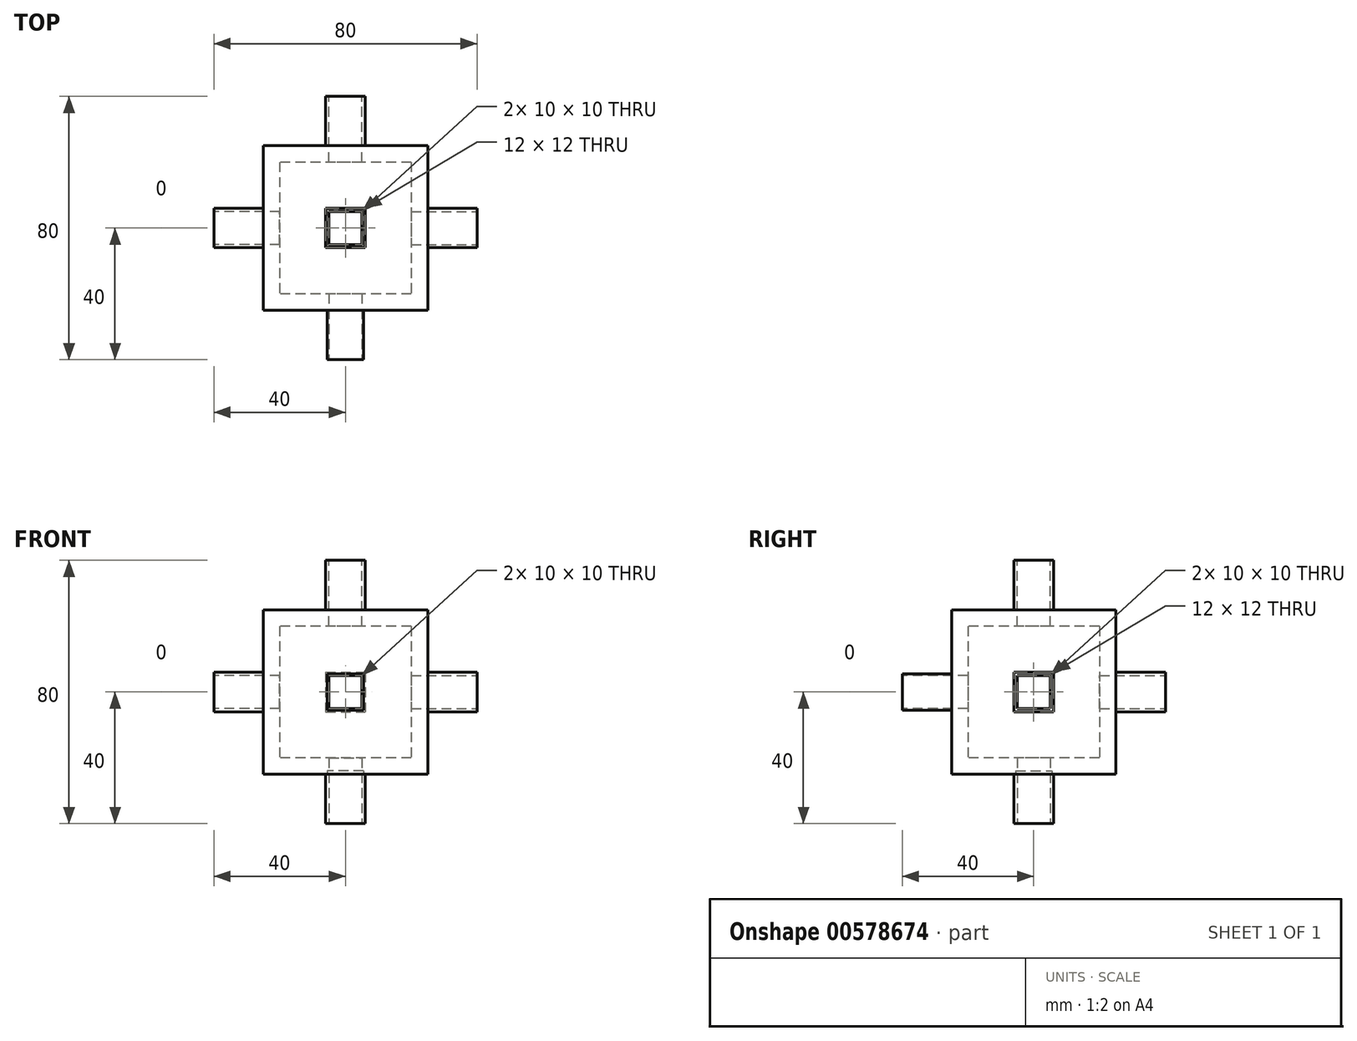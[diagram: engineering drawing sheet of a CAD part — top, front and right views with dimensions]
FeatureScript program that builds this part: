
annotation { "Feature Type Name" : "Feature", "Feature Type Description" : "" }
export const myFeature = defineFeature(function(context is Context, id is Id, definition is map)
    precondition{}
    {
        {
            var Q0;
            Q0=qCreatedBy(makeId("Top.planeOp"),FACE);
            var sketch = newSketch(context, id + "F0", { "sketchPlane" : qUnion([Q0])});
            skLineSegment(sketch, "E0.bottom", {"start": v(25, 25) * mm, "end": v(-25, 25) * mm});
            skLineSegment(sketch, "E0.top", {"start": v(25, -25) * mm, "end": v(-25, -25) * mm});
            skLineSegment(sketch, "E0.left", {"start": v(25, 25) * mm, "end": v(25, -25) * mm});
            skLineSegment(sketch, "E0.right", {"start": v(-25, 25) * mm, "end": v(-25, -25) * mm});
            skPoint(sketch, "E0.middle", {"position": v(0, 0) * mm});
            skLineSegment(sketch, "E1.0", {"start": v(20, -20) * mm, "end": v(-20, -20) * mm});
            skLineSegment(sketch, "E1.1", {"start": v(20, 20) * mm, "end": v(20, -20) * mm});
            skLineSegment(sketch, "E1.2", {"start": v(20, 20) * mm, "end": v(-20, 20) * mm});
            skLineSegment(sketch, "E1.3", {"start": v(-20, 20) * mm, "end": v(-20, -20) * mm});
            skSolve(sketch);
        }
        {
            var Q0;
            Q0=makeQuery(id+"F0.imprint","IMPRINT",FACE,{"disambiguationData":[TD([[makeQuery(id+"F0.imprint","IMPRINT",EDGE,{"derivedFrom":sQuery(id+"F0.wireOp",EDGE,"E0.bottom")}),1.0]])]});
            extrude(context, id + "F1", {"entities" : qUnion([Q0]), "depth" : 50 * mm, "offsetDistance" : 25 * mm});
        }
        {
            var Q0;
            Q0=makeQuery(id+"F0.imprint","IMPRINT",FACE,{"disambiguationData":[TD([[makeQuery(id+"F0.imprint","IMPRINT",EDGE,{"derivedFrom":sQuery(id+"F0.wireOp",EDGE,"E1.0")}),-1.0]])]});
            extrude(context, id + "F2", {"entities" : qUnion([Q0]), "operationType" : NewBodyOperationType.ADD, "depth" : 5 * mm, "offsetDistance" : 25 * mm});
        }
        {
            var Q0;
            Q0=makeQuery(id+"F1.opExtrude","CAP_FACE",FACE,{"disambiguationData":[OSD([sQuery(id+"F0.wireOp",EDGE,"E0.bottom"),sQuery(id+"F0.wireOp",EDGE,"E0.top"),sQuery(id+"F0.wireOp",EDGE,"E0.left"),sQuery(id+"F0.wireOp",EDGE,"E0.right"),sQuery(id+"F0.wireOp",EDGE,"E1.0"),sQuery(id+"F0.wireOp",EDGE,"E1.1"),sQuery(id+"F0.wireOp",EDGE,"E1.2"),sQuery(id+"F0.wireOp",EDGE,"E1.3")])],"isStart":false});
            var sketch = newSketch(context, id + "F3", { "sketchPlane" : qUnion([Q0])});
            skLineSegment(sketch, "E2.0", {"start": v(20, -20) * mm, "end": v(-20, -20) * mm});
            skLineSegment(sketch, "E3.0", {"start": v(-20, 20) * mm, "end": v(-20, -20) * mm});
            skLineSegment(sketch, "E4.0", {"start": v(20, 20) * mm, "end": v(-20, 20) * mm});
            skLineSegment(sketch, "E5.0", {"start": v(20, 20) * mm, "end": v(20, -20) * mm});
            skSolve(sketch);
        }
        {
            var Q0;
            Q0=makeQuery(id+"F3.imprint","IMPRINT",FACE,{"disambiguationData":[TD([[makeQuery(id+"F3.imprint","IMPRINT",EDGE,{"derivedFrom":sQuery(id+"F3.wireOp",EDGE,"E2.0")}),-1.0]])]});
            extrude(context, id + "F4", {"entities" : qUnion([Q0]), "operationType" : NewBodyOperationType.ADD, "oppositeDirection" : true, "depth" : 5 * mm, "offsetDistance" : 25 * mm});
        }
        {
            var Q0;
            Q0=makeQuery(id+"F1.opExtrude","CAP_FACE",FACE,{"disambiguationData":[OSD([sQuery(id+"F0.wireOp",EDGE,"E0.bottom"),sQuery(id+"F0.wireOp",EDGE,"E0.top"),sQuery(id+"F0.wireOp",EDGE,"E0.left"),sQuery(id+"F0.wireOp",EDGE,"E0.right")])],"isStart":false});
            var sketch = newSketch(context, id + "F5", { "sketchPlane" : qUnion([Q0])});
            skLineSegment(sketch, "E6.bottom", {"start": v(5, 5) * mm, "end": v(-5, 5) * mm});
            skLineSegment(sketch, "E6.top", {"start": v(5, -5) * mm, "end": v(-5, -5) * mm});
            skLineSegment(sketch, "E6.left", {"start": v(5, 5) * mm, "end": v(5, -5) * mm});
            skLineSegment(sketch, "E6.right", {"start": v(-5, 5) * mm, "end": v(-5, -5) * mm});
            skPoint(sketch, "E6.middle", {"position": v(0, 0) * mm});
            skSolve(sketch);
        }
        {
            var Q0;
            Q0=makeQuery(id+"F5.imprint","IMPRINT",FACE,{"disambiguationData":[TD([[makeQuery(id+"F5.imprint","IMPRINT",EDGE,{"derivedFrom":sQuery(id+"F5.wireOp",EDGE,"E6.bottom")}),1.0]])]});
            extrude(context, id + "F6", {"entities" : qUnion([Q0]), "operationType" : NewBodyOperationType.REMOVE, "oppositeDirection" : true, "depth" : 10 * mm, "offsetDistance" : 25 * mm});
        }
        {
            var Q0;
            Q0=makeQuery(id+"F1.opExtrude","SWEPT_FACE",FACE,{"disambiguationData":[OSD([sQuery(id+"F0.wireOp",EDGE,"E0.top")])]});
            var sketch = newSketch(context, id + "F7", { "sketchPlane" : qUnion([Q0])});
            skLineSegment(sketch, "E7.bottom", {"start": v(5, 30) * mm, "end": v(-5, 30) * mm});
            skLineSegment(sketch, "E7.top", {"start": v(5, 20) * mm, "end": v(-5, 20) * mm});
            skLineSegment(sketch, "E7.left", {"start": v(5, 30) * mm, "end": v(5, 20) * mm});
            skLineSegment(sketch, "E7.right", {"start": v(-5, 30) * mm, "end": v(-5, 20) * mm});
            skPoint(sketch, "E7.middle", {"position": v(0, 25) * mm});
            skLineSegment(sketch, "E8", {"start": v(-25, 25) * mm, "end": v(0, 25) * mm, "construction": true});
            skPoint(sketch, "E8.endSnap0", {"position": v(0, 50) * mm});
            skLineSegment(sketch, "E9", {"start": v(0, 25) * mm, "end": v(0, 50) * mm, "construction": true});
            skSolve(sketch);
        }
        {
            var Q0;
            Q0=makeQuery(id+"F7.imprint","IMPRINT",FACE,{"disambiguationData":[TD([[makeQuery(id+"F7.imprint","IMPRINT",EDGE,{"derivedFrom":sQuery(id+"F7.wireOp",EDGE,"E7.bottom")}),1.0]])]});
            extrude(context, id + "F8", {"entities" : qUnion([Q0]), "operationType" : NewBodyOperationType.REMOVE, "oppositeDirection" : true, "depth" : 10 * mm, "offsetDistance" : 25 * mm});
        }
        {
            var Q0;
            Q0=makeQuery(id+"F1.opExtrude","CAP_FACE",FACE,{"disambiguationData":[OSD([sQuery(id+"F0.wireOp",EDGE,"E0.bottom"),sQuery(id+"F0.wireOp",EDGE,"E0.top"),sQuery(id+"F0.wireOp",EDGE,"E0.left"),sQuery(id+"F0.wireOp",EDGE,"E0.right")])],"isStart":true});
            var sketch = newSketch(context, id + "F9", { "sketchPlane" : qUnion([Q0])});
            skLineSegment(sketch, "E10.bottom", {"start": v(5, 5) * mm, "end": v(-5, 5) * mm});
            skLineSegment(sketch, "E10.top", {"start": v(5, -5) * mm, "end": v(-5, -5) * mm});
            skLineSegment(sketch, "E10.left", {"start": v(5, 5) * mm, "end": v(5, -5) * mm});
            skLineSegment(sketch, "E10.right", {"start": v(-5, 5) * mm, "end": v(-5, -5) * mm});
            skPoint(sketch, "E10.middle", {"position": v(0, 0) * mm});
            skSolve(sketch);
        }
        {
            var Q0;
            Q0=makeQuery(id+"F9.imprint","IMPRINT",FACE,{"disambiguationData":[TD([[makeQuery(id+"F9.imprint","IMPRINT",EDGE,{"derivedFrom":sQuery(id+"F9.wireOp",EDGE,"E10.bottom")}),1.0]])]});
            extrude(context, id + "F10", {"entities" : qUnion([Q0]), "operationType" : NewBodyOperationType.REMOVE, "oppositeDirection" : true, "depth" : 10 * mm, "offsetDistance" : 25 * mm});
        }
        {
            var Q0;
            Q0=makeQuery(id+"F1.opExtrude","SWEPT_FACE",FACE,{"disambiguationData":[OSD([sQuery(id+"F0.wireOp",EDGE,"E0.bottom")])]});
            var sketch = newSketch(context, id + "F11", { "sketchPlane" : qUnion([Q0])});
            skLineSegment(sketch, "E11.bottom", {"start": v(5, 30) * mm, "end": v(-5, 30) * mm});
            skLineSegment(sketch, "E11.top", {"start": v(5, 20) * mm, "end": v(-5, 20) * mm});
            skLineSegment(sketch, "E11.left", {"start": v(5, 30) * mm, "end": v(5, 20) * mm});
            skLineSegment(sketch, "E11.right", {"start": v(-5, 30) * mm, "end": v(-5, 20) * mm});
            skPoint(sketch, "E11.middle", {"position": v(0, 25) * mm});
            skLineSegment(sketch, "E12", {"start": v(-25, 25) * mm, "end": v(0, 25) * mm, "construction": true});
            skPoint(sketch, "E12.endSnap0", {"position": v(0, 50) * mm});
            skLineSegment(sketch, "E13", {"start": v(0, 25) * mm, "end": v(0, 50) * mm, "construction": true});
            skSolve(sketch);
        }
        {
            var Q0;
            Q0=makeQuery(id+"F11.imprint","IMPRINT",FACE,{"disambiguationData":[TD([[makeQuery(id+"F11.imprint","IMPRINT",EDGE,{"derivedFrom":sQuery(id+"F11.wireOp",EDGE,"E11.bottom")}),1.0]])]});
            extrude(context, id + "F12", {"entities" : qUnion([Q0]), "operationType" : NewBodyOperationType.REMOVE, "oppositeDirection" : true, "depth" : 10 * mm, "offsetDistance" : 25 * mm});
        }
        {
            var Q0;
            Q0=makeQuery(id+"F1.opExtrude","SWEPT_FACE",FACE,{"disambiguationData":[OSD([sQuery(id+"F0.wireOp",EDGE,"E0.right")])]});
            var sketch = newSketch(context, id + "F13", { "sketchPlane" : qUnion([Q0])});
            skLineSegment(sketch, "E14", {"start": v(-25, 25) * mm, "end": v(0, 25) * mm, "construction": true});
            skPoint(sketch, "E14.endSnap0", {"position": v(0, 0) * mm});
            skLineSegment(sketch, "E15.bottom", {"start": v(-5, 30) * mm, "end": v(5, 30) * mm});
            skLineSegment(sketch, "E15.top", {"start": v(-5, 20) * mm, "end": v(5, 20) * mm});
            skLineSegment(sketch, "E15.left", {"start": v(-5, 30) * mm, "end": v(-5, 20) * mm});
            skLineSegment(sketch, "E15.right", {"start": v(5, 30) * mm, "end": v(5, 20) * mm});
            skPoint(sketch, "E15.middle", {"position": v(0, 25) * mm});
            skSolve(sketch);
        }
        {
            var Q0;
            Q0=makeQuery(id+"F13.imprint","IMPRINT",FACE,{"disambiguationData":[TD([[makeQuery(id+"F13.imprint","IMPRINT",EDGE,{"derivedFrom":sQuery(id+"F13.wireOp",EDGE,"E15.bottom")}),-1.0]])]});
            extrude(context, id + "F14", {"entities" : qUnion([Q0]), "operationType" : NewBodyOperationType.REMOVE, "oppositeDirection" : true, "depth" : 10 * mm, "offsetDistance" : 25 * mm});
        }
        {
            var Q0;
            Q0=makeQuery(id+"F1.opExtrude","SWEPT_FACE",FACE,{"disambiguationData":[OSD([sQuery(id+"F0.wireOp",EDGE,"E0.left")])]});
            var sketch = newSketch(context, id + "F15", { "sketchPlane" : qUnion([Q0])});
            skLineSegment(sketch, "E16.bottom", {"start": v(5, 30) * mm, "end": v(-5, 30) * mm});
            skLineSegment(sketch, "E16.top", {"start": v(5, 20) * mm, "end": v(-5, 20) * mm});
            skLineSegment(sketch, "E16.left", {"start": v(5, 30) * mm, "end": v(5, 20) * mm});
            skLineSegment(sketch, "E16.right", {"start": v(-5, 30) * mm, "end": v(-5, 20) * mm});
            skPoint(sketch, "E16.middle", {"position": v(0, 25) * mm});
            skPoint(sketch, "E16.middle.positionSnap0", {"position": v(0, 0) * mm});
            skPoint(sketch, "E16.middle.positionSnap1", {"position": v(-25, 25) * mm});
            skPoint(sketch, "E16.centerSnap0", {"position": v(0, 0) * mm});
            skPoint(sketch, "E16.centerSnap1", {"position": v(-25, 25) * mm});
            skSolve(sketch);
        }
        {
            var Q0;
            Q0=makeQuery(id+"F15.imprint","IMPRINT",FACE,{"disambiguationData":[TD([[makeQuery(id+"F15.imprint","IMPRINT",EDGE,{"derivedFrom":sQuery(id+"F15.wireOp",EDGE,"E16.bottom")}),1.0]])]});
            extrude(context, id + "F16", {"entities" : qUnion([Q0]), "operationType" : NewBodyOperationType.REMOVE, "oppositeDirection" : true, "depth" : 10 * mm, "offsetDistance" : 25 * mm});
        }
        {
            var Q0;
            Q0=makeQuery(id+"F1.opExtrude","SWEPT_FACE",FACE,{"disambiguationData":[OSD([sQuery(id+"F0.wireOp",EDGE,"E0.top")])]});
            var sketch = newSketch(context, id + "F17", { "sketchPlane" : qUnion([Q0])});
            skLineSegment(sketch, "E17.bottom", {"start": v(-5.5, 19.5) * mm, "end": v(5.5, 19.5) * mm});
            skLineSegment(sketch, "E17.top", {"start": v(-5.5, 30.5) * mm, "end": v(5.5, 30.5) * mm});
            skLineSegment(sketch, "E17.left", {"start": v(-5.5, 19.5) * mm, "end": v(-5.5, 30.5) * mm});
            skLineSegment(sketch, "E17.right", {"start": v(5.5, 19.5) * mm, "end": v(5.5, 30.5) * mm});
            skPoint(sketch, "E17.middle", {"position": v(0, 25) * mm});
            skPoint(sketch, "E17.middle.positionSnap0", {"position": v(-5, 25) * mm});
            skPoint(sketch, "E17.middle.positionSnap1", {"position": v(0, 30) * mm});
            skPoint(sketch, "E17.centerSnap0", {"position": v(-5, 25) * mm});
            skPoint(sketch, "E17.centerSnap1", {"position": v(0, 30) * mm});
            skSolve(sketch);
        }
        {
            var Q0;
            Q0=makeQuery(id+"F17.imprint","IMPRINT",FACE,{"disambiguationData":[TD([[makeQuery(id+"F17.imprint","IMPRINT",EDGE,{"derivedFrom":sQuery(id+"F17.wireOp",EDGE,"E17.bottom")}),1.0]])]});
            extrude(context, id + "F18", {"entities" : qUnion([Q0]), "operationType" : NewBodyOperationType.ADD, "depth" : 15 * mm, "offsetDistance" : 25 * mm});
        }
        {
            var Q0;
            Q0=makeQuery(id+"F4.boolean.opBoolean","MERGE",FACE,{"derivedFrom":[makeQuery(id+"F1.opExtrude","CAP_FACE",FACE,{"disambiguationData":[OSD([sQuery(id+"F0.wireOp",EDGE,"E0.bottom"),sQuery(id+"F0.wireOp",EDGE,"E0.top"),sQuery(id+"F0.wireOp",EDGE,"E0.left"),sQuery(id+"F0.wireOp",EDGE,"E0.right"),sQuery(id+"F0.wireOp",EDGE,"E1.0"),sQuery(id+"F0.wireOp",EDGE,"E1.1"),sQuery(id+"F0.wireOp",EDGE,"E1.2"),sQuery(id+"F0.wireOp",EDGE,"E1.3")])],"isStart":false}),makeQuery(id+"F4.opExtrude","CAP_FACE",FACE,{"disambiguationData":[OSD([sQuery(id+"F3.wireOp",EDGE,"E2.0"),sQuery(id+"F3.wireOp",EDGE,"E3.0"),sQuery(id+"F3.wireOp",EDGE,"E4.0"),sQuery(id+"F3.wireOp",EDGE,"E5.0")])],"isStart":true})]});
            var sketch = newSketch(context, id + "F19", { "sketchPlane" : qUnion([Q0])});
            skLineSegment(sketch, "E18.0", {"start": v(5, 5) * mm, "end": v(-5, 5) * mm});
            skLineSegment(sketch, "E19.0", {"start": v(5, 5) * mm, "end": v(5, -5) * mm});
            skLineSegment(sketch, "E20.0", {"start": v(5, -5) * mm, "end": v(-5, -5) * mm});
            skLineSegment(sketch, "E21.0", {"start": v(-5, 5) * mm, "end": v(-5, -5) * mm});
            skLineSegment(sketch, "E22.0", {"start": v(6, -6) * mm, "end": v(-6, -6) * mm});
            skLineSegment(sketch, "E22.1", {"start": v(6, 6) * mm, "end": v(6, -6) * mm});
            skLineSegment(sketch, "E22.2", {"start": v(6, 6) * mm, "end": v(-6, 6) * mm});
            skLineSegment(sketch, "E22.3", {"start": v(-6, 6) * mm, "end": v(-6, -6) * mm});
            skSolve(sketch);
        }
        {
            var Q0;
            Q0=makeQuery(id+"F19.imprint","IMPRINT",FACE,{"disambiguationData":[TD([[makeQuery(id+"F19.imprint","IMPRINT",EDGE,{"derivedFrom":sQuery(id+"F19.wireOp",EDGE,"E18.0")}),-1.0]])]});
            extrude(context, id + "F20", {"entities" : qUnion([Q0]), "operationType" : NewBodyOperationType.ADD, "depth" : 15 * mm, "offsetDistance" : 25 * mm});
        }
        {
            var Q0;
            Q0=makeQuery(id+"F1.opExtrude","SWEPT_FACE",FACE,{"disambiguationData":[OSD([sQuery(id+"F0.wireOp",EDGE,"E0.bottom")])]});
            var sketch = newSketch(context, id + "F21", { "sketchPlane" : qUnion([Q0])});
            skLineSegment(sketch, "E23.0", {"start": v(5, 20) * mm, "end": v(-5, 20) * mm});
            skLineSegment(sketch, "E24.0", {"start": v(-5, 30) * mm, "end": v(-5, 20) * mm});
            skLineSegment(sketch, "E25.0", {"start": v(5, 30) * mm, "end": v(-5, 30) * mm});
            skLineSegment(sketch, "E26.0", {"start": v(5, 30) * mm, "end": v(5, 20) * mm});
            skLineSegment(sketch, "E27.0", {"start": v(6, 31) * mm, "end": v(6, 19) * mm});
            skLineSegment(sketch, "E27.1", {"start": v(6, 31) * mm, "end": v(-6, 31) * mm});
            skLineSegment(sketch, "E27.2", {"start": v(-6, 31) * mm, "end": v(-6, 19) * mm});
            skLineSegment(sketch, "E27.3", {"start": v(6, 19) * mm, "end": v(-6, 19) * mm});
            skSolve(sketch);
        }
        {
            var Q0;
            Q0 = qSketchRegion(id + "F21", true);
            extrude(context, id + "F22", {"entities" : qUnion([Q0]), "operationType" : NewBodyOperationType.ADD, "depth" : 15 * mm, "offsetDistance" : 25 * mm});
        }
        {
            var Q0;
            Q0=makeQuery(id+"F0.imprint","IMPRINT",FACE,{"disambiguationData":[TD([[makeQuery(id+"F0.imprint","IMPRINT",EDGE,{"derivedFrom":sQuery(id+"F0.wireOp",EDGE,"E1.0")}),-1.0]])]});
            var sketch = newSketch(context, id + "F23", { "sketchPlane" : qUnion([Q0])});
            skLineSegment(sketch, "E28.0", {"start": v(5, -5) * mm, "end": v(-5, -5) * mm});
            skLineSegment(sketch, "E29.0", {"start": v(-5, -5) * mm, "end": v(-5, 5) * mm});
            skLineSegment(sketch, "E30.0", {"start": v(5, 5) * mm, "end": v(-5, 5) * mm});
            skLineSegment(sketch, "E31.0", {"start": v(5, -5) * mm, "end": v(5, 5) * mm});
            skLineSegment(sketch, "E32.0", {"start": v(6, -6) * mm, "end": v(-6, -6) * mm});
            skLineSegment(sketch, "E32.1", {"start": v(6, -6) * mm, "end": v(6, 6) * mm});
            skLineSegment(sketch, "E32.2", {"start": v(6, 6) * mm, "end": v(-6, 6) * mm});
            skLineSegment(sketch, "E32.3", {"start": v(-6, -6) * mm, "end": v(-6, 6) * mm});
            skSolve(sketch);
        }
        {
            var Q0;
            Q0=makeQuery(id+"F23.imprint","IMPRINT",FACE,{"disambiguationData":[TD([[makeQuery(id+"F23.imprint","IMPRINT",EDGE,{"derivedFrom":sQuery(id+"F23.wireOp",EDGE,"E28.0")}),1.0]])]});
            extrude(context, id + "F24", {"entities" : qUnion([Q0]), "operationType" : NewBodyOperationType.ADD, "oppositeDirection" : true, "depth" : 15 * mm, "offsetDistance" : 25 * mm});
        }
        {
            var Q0;
            Q0=makeQuery(id+"F1.opExtrude","SWEPT_FACE",FACE,{"disambiguationData":[OSD([sQuery(id+"F0.wireOp",EDGE,"E0.left")])]});
            var sketch = newSketch(context, id + "F25", { "sketchPlane" : qUnion([Q0])});
            skLineSegment(sketch, "E33.0", {"start": v(-5, 30) * mm, "end": v(-5, 20) * mm});
            skLineSegment(sketch, "E34.0", {"start": v(5, 20) * mm, "end": v(-5, 20) * mm});
            skLineSegment(sketch, "E35.0", {"start": v(5, 30) * mm, "end": v(5, 20) * mm});
            skLineSegment(sketch, "E36.0", {"start": v(5, 30) * mm, "end": v(-5, 30) * mm});
            skLineSegment(sketch, "E37.0", {"start": v(6, 31) * mm, "end": v(-6, 31) * mm});
            skLineSegment(sketch, "E37.1", {"start": v(6, 31) * mm, "end": v(6, 19) * mm});
            skLineSegment(sketch, "E37.2", {"start": v(6, 19) * mm, "end": v(-6, 19) * mm});
            skLineSegment(sketch, "E37.3", {"start": v(-6, 31) * mm, "end": v(-6, 19) * mm});
            skSolve(sketch);
        }
        {
            var Q0;
            Q0=makeQuery(id+"F25.imprint","IMPRINT",FACE,{"disambiguationData":[TD([[makeQuery(id+"F25.imprint","IMPRINT",EDGE,{"derivedFrom":sQuery(id+"F25.wireOp",EDGE,"E33.0")}),-1.0]])]});
            extrude(context, id + "F26", {"entities" : qUnion([Q0]), "operationType" : NewBodyOperationType.ADD, "depth" : 15 * mm, "offsetDistance" : 25 * mm});
        }
        {
            var Q0;
            Q0=makeQuery(id+"F1.opExtrude","SWEPT_FACE",FACE,{"disambiguationData":[OSD([sQuery(id+"F0.wireOp",EDGE,"E0.right")])]});
            var sketch = newSketch(context, id + "F27", { "sketchPlane" : qUnion([Q0])});
            skLineSegment(sketch, "E38.0", {"start": v(-5, 30) * mm, "end": v(5, 30) * mm});
            skLineSegment(sketch, "E39.0", {"start": v(-5, 30) * mm, "end": v(-5, 20) * mm});
            skLineSegment(sketch, "E40.0", {"start": v(-5, 20) * mm, "end": v(5, 20) * mm});
            skLineSegment(sketch, "E41.0", {"start": v(5, 30) * mm, "end": v(5, 20) * mm});
            skLineSegment(sketch, "E42.0", {"start": v(-6, 31) * mm, "end": v(6, 31) * mm});
            skLineSegment(sketch, "E42.1", {"start": v(-6, 31) * mm, "end": v(-6, 19) * mm});
            skLineSegment(sketch, "E42.2", {"start": v(-6, 19) * mm, "end": v(6, 19) * mm});
            skLineSegment(sketch, "E42.3", {"start": v(6, 31) * mm, "end": v(6, 19) * mm});
            skSolve(sketch);
        }
        {
            var Q0;
            Q0=makeQuery(id+"F27.imprint","IMPRINT",FACE,{"disambiguationData":[TD([[makeQuery(id+"F27.imprint","IMPRINT",EDGE,{"derivedFrom":sQuery(id+"F27.wireOp",EDGE,"E38.0")}),1.0]])]});
            extrude(context, id + "F28", {"entities" : qUnion([Q0]), "operationType" : NewBodyOperationType.ADD, "depth" : 15 * mm, "offsetDistance" : 25 * mm});
        }
        {
            var Q0;
            Q0=qCreatedBy(makeId("Top.planeOp"),FACE);
            var sketch = newSketch(context, id + "F29", { "sketchPlane" : qUnion([Q0])});
            skLineSegment(sketch, "E43.bottom", {"start": v(5.5, -5.5) * mm, "end": v(-5.5, -5.5) * mm});
            skLineSegment(sketch, "E43.top", {"start": v(5.5, 5.5) * mm, "end": v(-5.5, 5.5) * mm});
            skLineSegment(sketch, "E43.left", {"start": v(5.5, -5.5) * mm, "end": v(5.5, 5.5) * mm});
            skLineSegment(sketch, "E43.right", {"start": v(-5.5, -5.5) * mm, "end": v(-5.5, 5.5) * mm});
            skPoint(sketch, "E43.middle", {"position": v(0, 0) * mm});
            skSolve(sketch);
        }
        {
            var Q0;
            Q0=makeQuery(id+"F29.imprint","IMPRINT",FACE,{"disambiguationData":[TD([[makeQuery(id+"F29.imprint","IMPRINT",EDGE,{"derivedFrom":sQuery(id+"F29.wireOp",EDGE,"E43.bottom")}),-1.0]])]});
            extrude(context, id + "F30", {"entities" : qUnion([Q0]), "depth" : 1 * mm, "offsetDistance" : 25 * mm});
        }
    });
